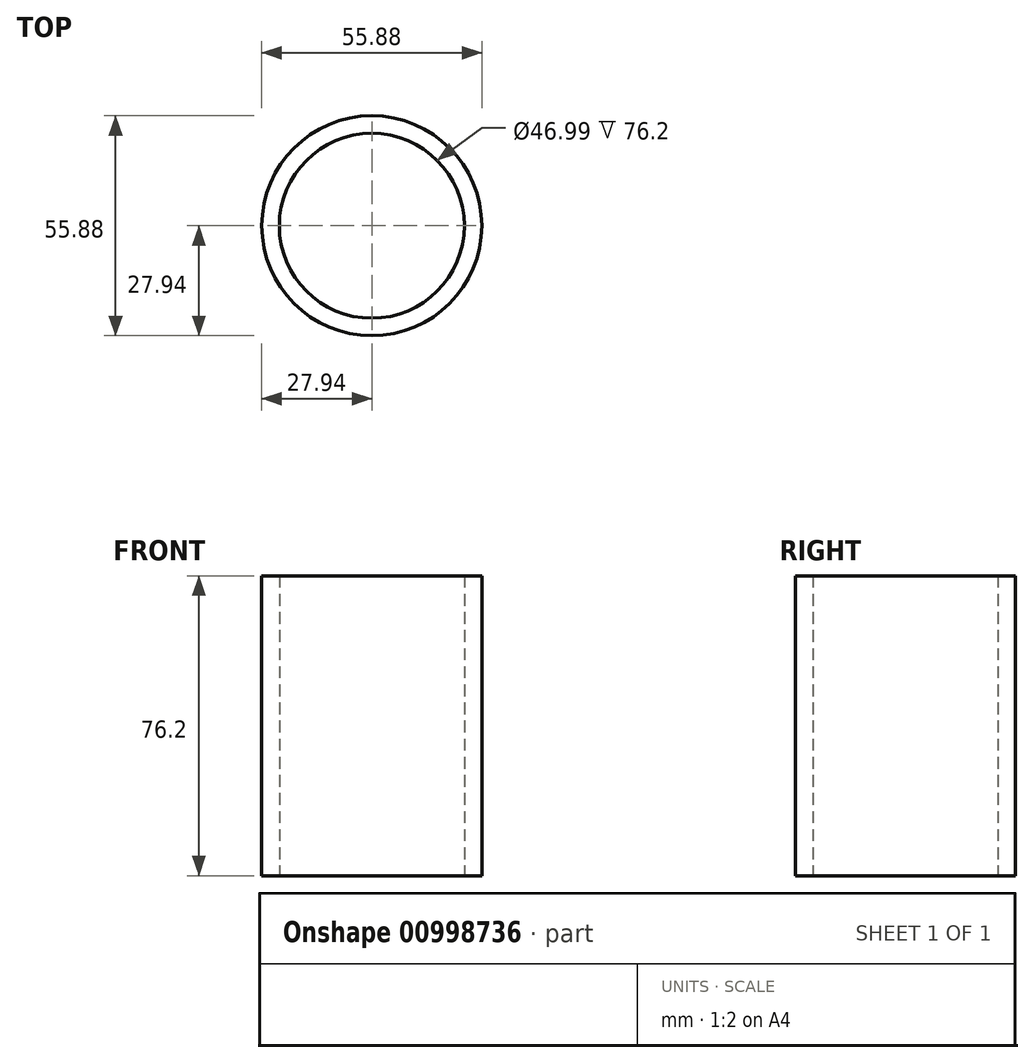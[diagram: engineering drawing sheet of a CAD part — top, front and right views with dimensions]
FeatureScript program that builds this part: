
annotation { "Feature Type Name" : "Feature", "Feature Type Description" : "" }
export const myFeature = defineFeature(function(context is Context, id is Id, definition is map)
    precondition{}
    {
        {
            var Q0;
            Q0=qCreatedBy(makeId("Top.planeOp"),FACE);
            var sketch = newSketch(context, id + "F0", { "sketchPlane" : qUnion([Q0])});
            skCircle(sketch, "E0", {"center": v(0, 0) * mm, "radius": 23.5 * mm});
            skCircle(sketch, "E1", {"center": v(0, 0) * mm, "radius": 27.94 * mm});
            skSolve(sketch);
        }
        {
            var Q0;
            Q0 = qSketchRegion(id + "F0", true);
            extrude(context, id + "F1", {"entities" : qUnion([Q0]), "depth" : 76.2 * mm, "offsetDistance" : 25.4 * mm});
        }
    });
